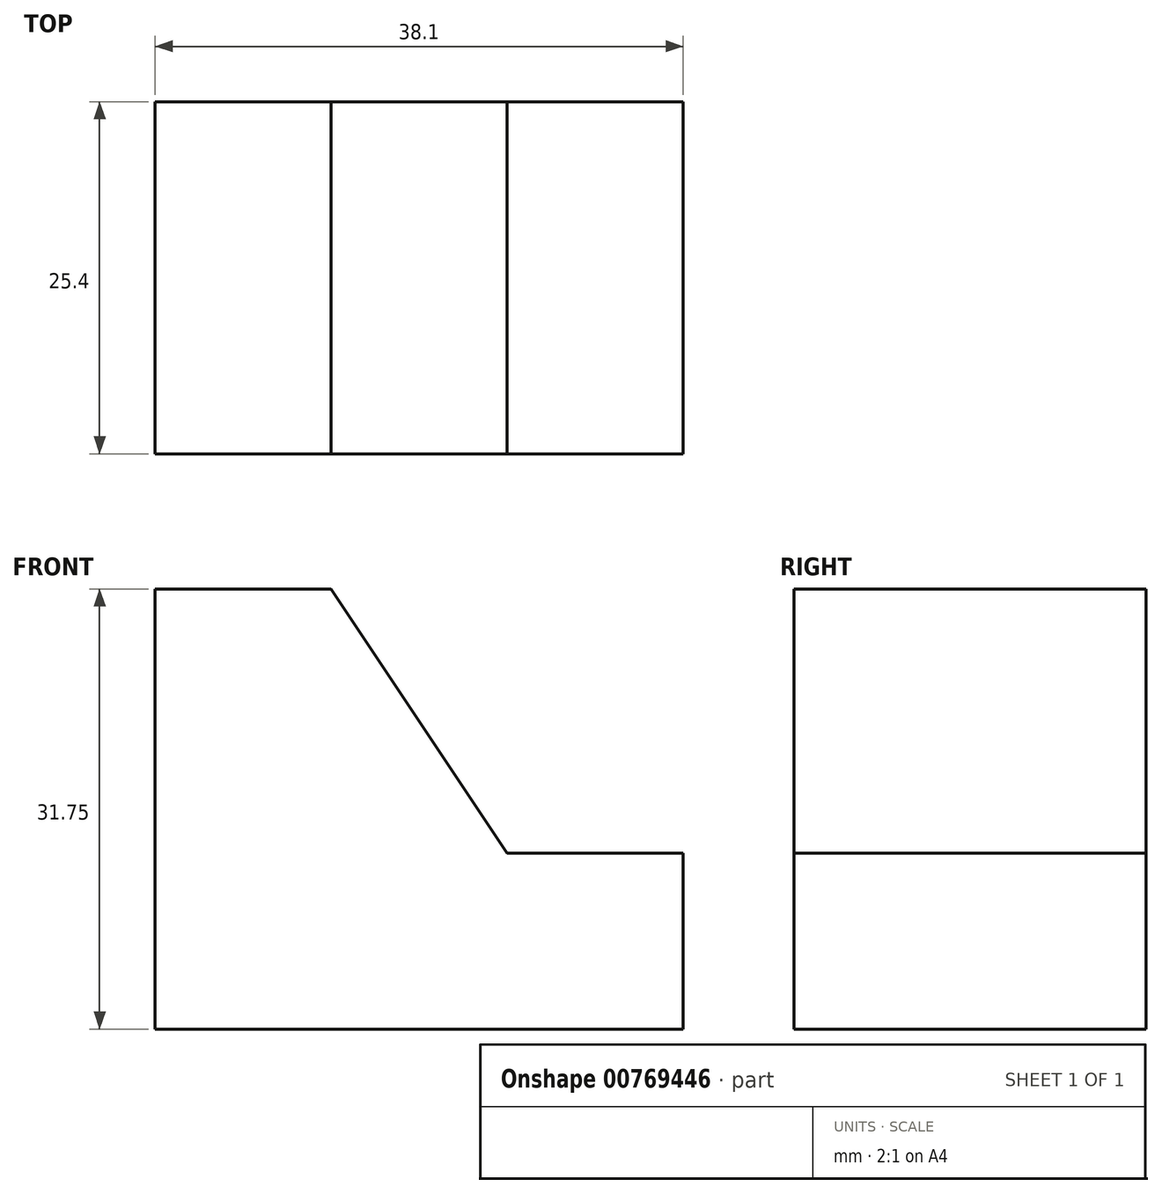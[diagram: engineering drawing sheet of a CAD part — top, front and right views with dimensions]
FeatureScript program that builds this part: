
annotation { "Feature Type Name" : "Feature", "Feature Type Description" : "" }
export const myFeature = defineFeature(function(context is Context, id is Id, definition is map)
    precondition{}
    {
        {
            var Q0;
            Q0=qCreatedBy(makeId("Front.planeOp"),FACE);
            var sketch = newSketch(context, id + "F0", { "sketchPlane" : qUnion([Q0])});
            skLineSegment(sketch, "E0", {"start": v(0, 0) * mm, "end": v(38.1, 0) * mm});
            skLineSegment(sketch, "E1", {"start": v(0, 0) * mm, "end": v(0, 31.75) * mm});
            skLineSegment(sketch, "E2", {"start": v(0, 31.75) * mm, "end": v(12.7, 31.75) * mm});
            skLineSegment(sketch, "E3", {"start": v(38.1, 0) * mm, "end": v(38.1, 12.7) * mm});
            skLineSegment(sketch, "E4", {"start": v(38.1, 12.7) * mm, "end": v(25.4, 12.7) * mm});
            skLineSegment(sketch, "E5", {"start": v(25.4, 12.7) * mm, "end": v(12.7, 31.75) * mm});
            skSolve(sketch);
        }
        {
            var Q0;
            Q0=makeQuery(id+"F0.imprint","IMPRINT",FACE,{"disambiguationData":[TD([[makeQuery(id+"F0.imprint","IMPRINT",EDGE,{"derivedFrom":sQuery(id+"F0.wireOp",EDGE,"E0")}),1.0]])]});
            extrude(context, id + "F1", {"entities" : qUnion([Q0]), "depth" : 25.4 * mm, "offsetDistance" : 25.4 * mm});
        }
    });
